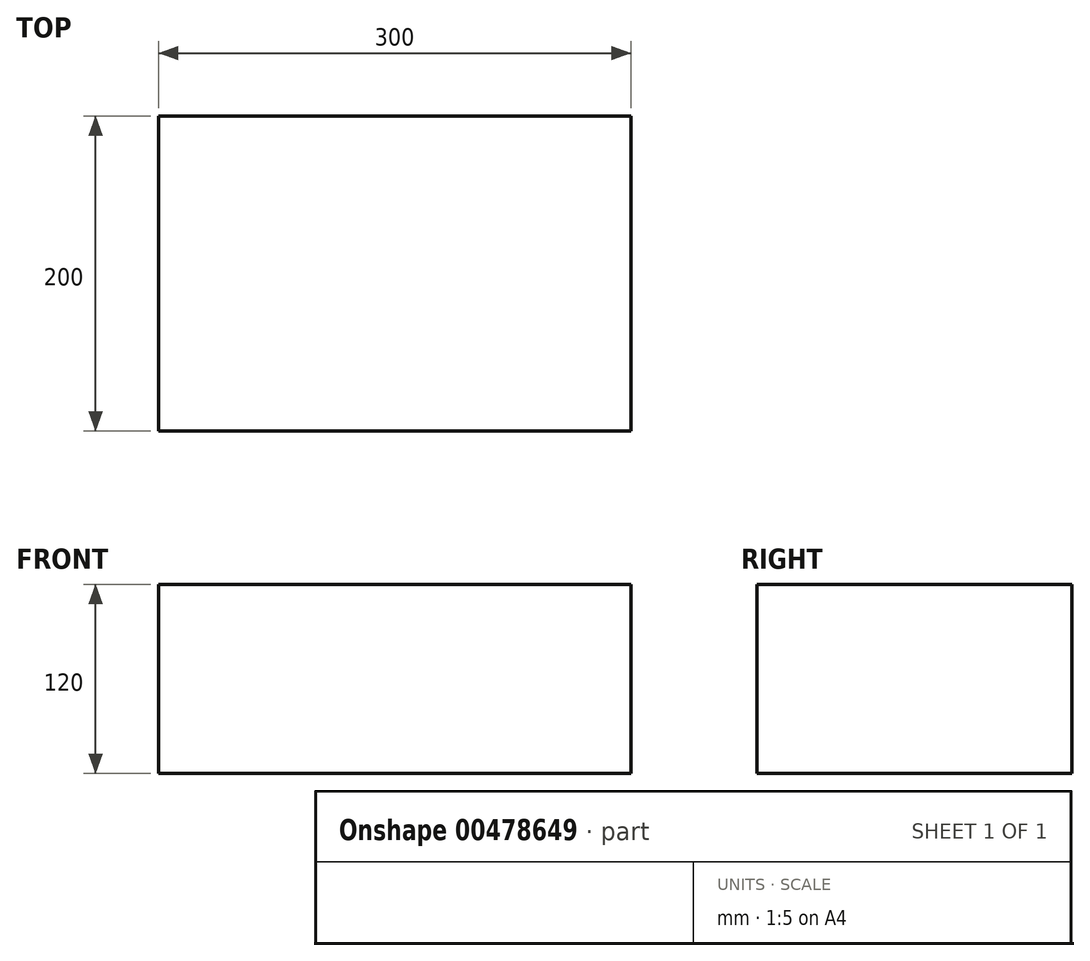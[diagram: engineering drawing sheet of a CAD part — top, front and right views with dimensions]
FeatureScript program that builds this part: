
annotation { "Feature Type Name" : "Feature", "Feature Type Description" : "" }
export const myFeature = defineFeature(function(context is Context, id is Id, definition is map)
    precondition{}
    {
        {
            var Q0;
            Q0=qCreatedBy(makeId("Top.planeOp"),FACE);
            var sketch = newSketch(context, id + "F0", { "sketchPlane" : qUnion([Q0])});
            skLineSegment(sketch, "E0", {"start": v(-300, 126.16) * mm, "end": v(-300, -73.84) * mm});
            skLineSegment(sketch, "E1", {"start": v(-300, 126.16) * mm, "end": v(0, 126.16) * mm});
            skLineSegment(sketch, "E2", {"start": v(0, 126.16) * mm, "end": v(0, -73.84) * mm});
            skLineSegment(sketch, "E3", {"start": v(0, -73.84) * mm, "end": v(-300, -73.84) * mm});
            skSolve(sketch);
        }
        {
            var Q0;
            Q0 = qSketchRegion(id + "F0", true);
            extrude(context, id + "F1", {"entities" : qUnion([Q0]), "depth" : 120 * mm});
        }
    });
